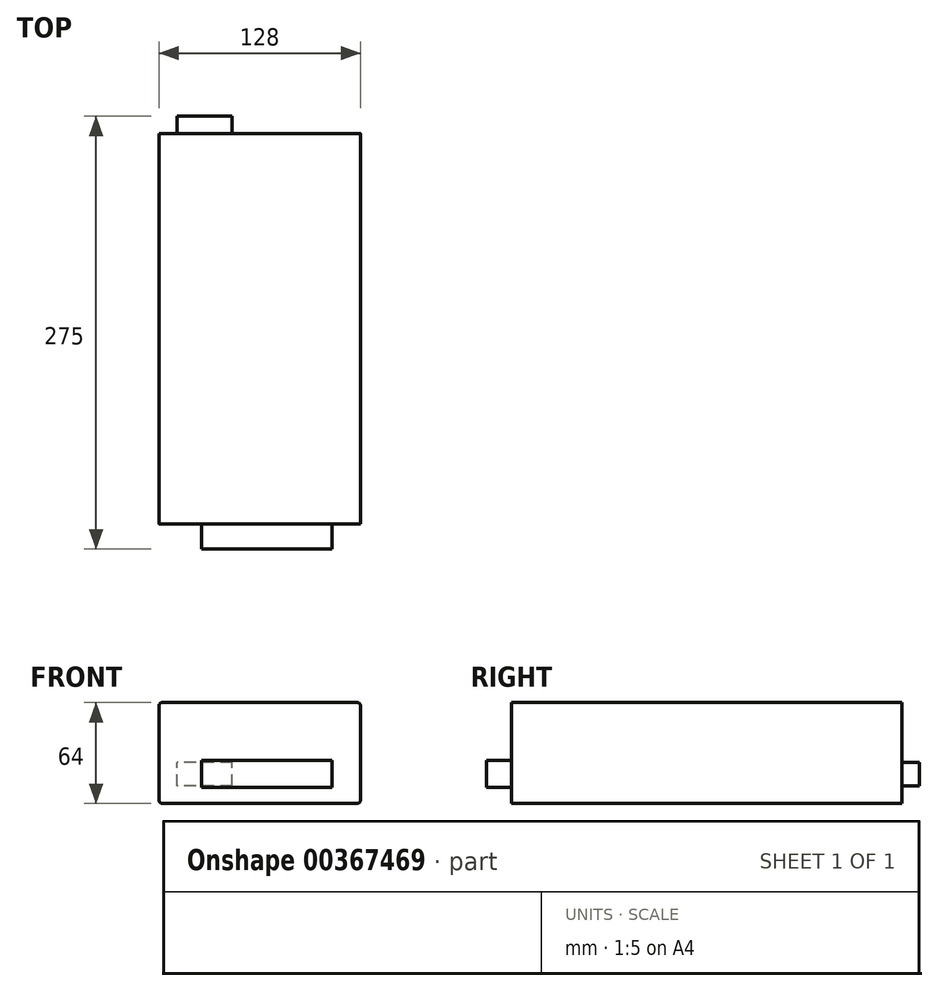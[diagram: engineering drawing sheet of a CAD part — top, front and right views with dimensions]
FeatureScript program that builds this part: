
annotation { "Feature Type Name" : "Feature", "Feature Type Description" : "" }
export const myFeature = defineFeature(function(context is Context, id is Id, definition is map)
    precondition{}
    {
        {
            var Q0;
            Q0=qCreatedBy(makeId("Front.planeOp"),FACE);
            var sketch = newSketch(context, id + "F0", { "sketchPlane" : qUnion([Q0])});
            skLineSegment(sketch, "E0.bottom", {"start": v(0, 0) * mm, "end": v(128, 0) * mm});
            skLineSegment(sketch, "E0.top", {"start": v(0, 64) * mm, "end": v(128, 64) * mm});
            skLineSegment(sketch, "E0.left", {"start": v(0, 0) * mm, "end": v(0, 64) * mm});
            skLineSegment(sketch, "E0.right", {"start": v(128, 0) * mm, "end": v(128, 64) * mm});
            skSolve(sketch);
        }
        {
            var Q0;
            Q0=qSketchRegion(id+"F0",true);
            extrude(context, id + "F1", {"entities" : qUnion([Q0]), "depth" : 248 * mm});
        }
        {
            var Q0;
            Q0=makeQuery(id+"F1.opExtrude","CAP_FACE",FACE,{"disambiguationData":[OSD([sQuery(id+"F0.wireOp",EDGE,"E0.bottom"),sQuery(id+"F0.wireOp",EDGE,"E0.top"),sQuery(id+"F0.wireOp",EDGE,"E0.left"),sQuery(id+"F0.wireOp",EDGE,"E0.right")])],"isStart":false});
            var sketch = newSketch(context, id + "F2", { "sketchPlane" : qUnion([Q0])});
            skLineSegment(sketch, "E1", {"start": v(110, 10) * mm, "end": v(27, 10) * mm});
            skLineSegment(sketch, "E2", {"start": v(27, 10) * mm, "end": v(27, 27.33) * mm});
            skLineSegment(sketch, "E3", {"start": v(27, 27.33) * mm, "end": v(110, 27.33) * mm});
            skLineSegment(sketch, "E4", {"start": v(110, 27.33) * mm, "end": v(110, 10) * mm});
            skSolve(sketch);
        }
        {
            var Q0;
            Q0=qSketchRegion(id+"F2",true);
            extrude(context, id + "F3", {"entities" : qUnion([Q0]), "operationType" : NewBodyOperationType.ADD, "depth" : 16 * mm});
        }
        {
            var Q0;
            Q0=makeQuery(id+"F1.opExtrude","CAP_FACE",FACE,{"disambiguationData":[OSD([sQuery(id+"F0.wireOp",EDGE,"E0.bottom"),sQuery(id+"F0.wireOp",EDGE,"E0.top"),sQuery(id+"F0.wireOp",EDGE,"E0.left"),sQuery(id+"F0.wireOp",EDGE,"E0.right")])],"isStart":true});
            var sketch = newSketch(context, id + "F4", { "sketchPlane" : qUnion([Q0])});
            skLineSegment(sketch, "E5.bottom", {"start": v(-46.5, 11) * mm, "end": v(-11.5, 11) * mm});
            skLineSegment(sketch, "E5.top", {"start": v(-46.5, 26) * mm, "end": v(-11.5, 26) * mm});
            skLineSegment(sketch, "E5.left", {"start": v(-46.5, 11) * mm, "end": v(-46.5, 26) * mm});
            skLineSegment(sketch, "E5.right", {"start": v(-11.5, 11) * mm, "end": v(-11.5, 26) * mm});
            skSolve(sketch);
        }
        {
            var Q0;
            Q0=qSketchRegion(id+"F4",true);
            extrude(context, id + "F5", {"entities" : qUnion([Q0]), "operationType" : NewBodyOperationType.ADD, "depth" : 11 * mm});
        }
        {
            var Q0;
            Q0=makeQuery(id+"F1.opExtrude","SWEPT_EDGE",EDGE,{"disambiguationData":[OSD([sQuery(id+"F0.wireOp",EDGE,"E0.top"),sQuery(id+"F0.wireOp",EDGE,"E0.right")])]});
            var Q1;
            Q1=makeQuery(id+"F1.opExtrude","SWEPT_EDGE",EDGE,{"disambiguationData":[OSD([sQuery(id+"F0.wireOp",EDGE,"E0.bottom"),sQuery(id+"F0.wireOp",EDGE,"E0.right")])]});
            var Q2;
            Q2=makeQuery(id+"F1.opExtrude","SWEPT_EDGE",EDGE,{"disambiguationData":[OSD([sQuery(id+"F0.wireOp",EDGE,"E0.top"),sQuery(id+"F0.wireOp",EDGE,"E0.left")])]});
            var Q3;
            Q3=makeQuery(id+"F1.opExtrude","SWEPT_EDGE",EDGE,{"disambiguationData":[OSD([sQuery(id+"F0.wireOp",EDGE,"E0.bottom"),sQuery(id+"F0.wireOp",EDGE,"E0.left")])]});
            fillet(context, id + "F6", {"entities" : qUnion([Q0, Q1, Q2, Q3]), "radius" : 2 * mm, "tangentPropagation" : true, "allowEdgeOverflow" : false});
        }
    });
